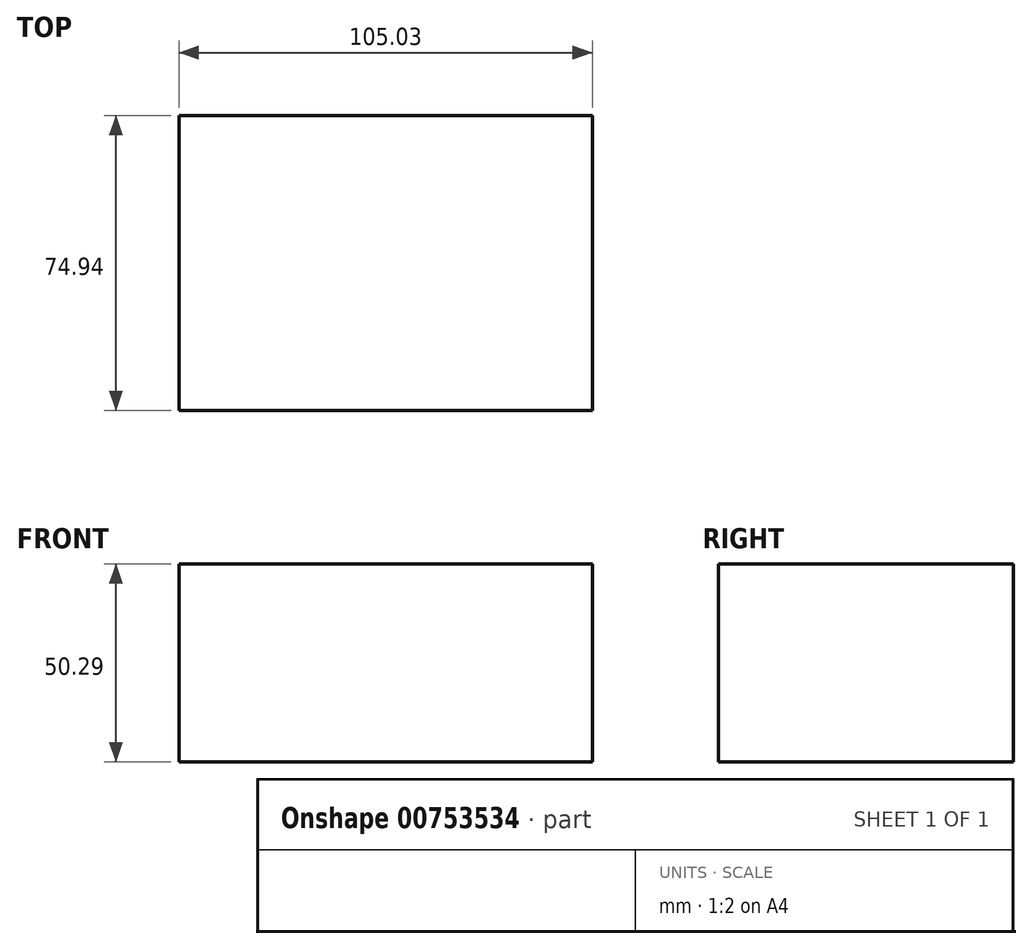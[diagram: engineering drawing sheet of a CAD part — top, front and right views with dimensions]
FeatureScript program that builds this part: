
annotation { "Feature Type Name" : "Feature", "Feature Type Description" : "" }
export const myFeature = defineFeature(function(context is Context, id is Id, definition is map)
    precondition{}
    {
        {
            var Q0;
            Q0=qCreatedBy(makeId("Top.planeOp"),FACE);
            var sketch = newSketch(context, id + "F0", { "sketchPlane" : qUnion([Q0])});
            skLineSegment(sketch, "E0.bottom", {"start": v(-46.12, 0) * mm, "end": v(58.9, 0) * mm});
            skLineSegment(sketch, "E0.top", {"start": v(-46.12, -74.94) * mm, "end": v(58.9, -74.94) * mm});
            skLineSegment(sketch, "E0.left", {"start": v(-46.12, 0) * mm, "end": v(-46.12, -74.94) * mm});
            skLineSegment(sketch, "E0.right", {"start": v(58.9, 0) * mm, "end": v(58.9, -74.94) * mm});
            skSolve(sketch);
        }
        {
            var Q0;
            Q0=makeQuery(id+"F0.imprint","IMPRINT",FACE,{"disambiguationData":[TD([[makeQuery(id+"F0.imprint","IMPRINT",EDGE,{"derivedFrom":sQuery(id+"F0.wireOp",EDGE,"E0.bottom")}),-1.0]])]});
            extrude(context, id + "F1", {"entities" : qUnion([Q0]), "depth" : 50.3 * mm, "offsetDistance" : 25.4 * mm});
        }
    });
